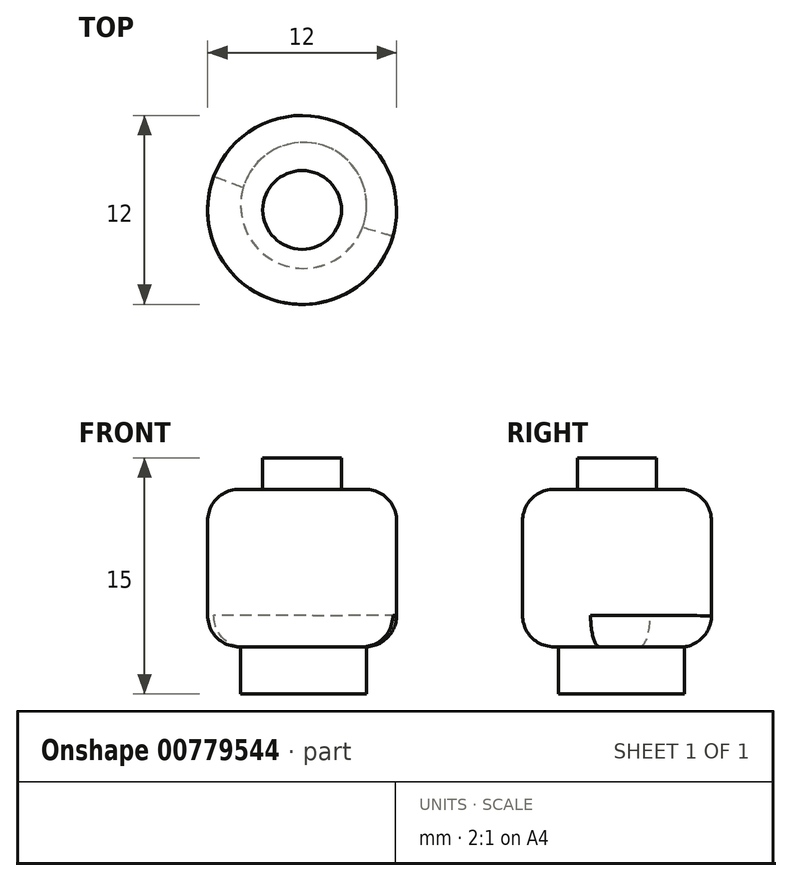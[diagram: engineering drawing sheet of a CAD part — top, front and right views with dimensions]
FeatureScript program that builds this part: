
annotation { "Feature Type Name" : "Feature", "Feature Type Description" : "" }
export const myFeature = defineFeature(function(context is Context, id is Id, definition is map)
    precondition{}
    {
        {
            var Q0;
            Q0=qCreatedBy(makeId("Top.planeOp"),FACE);
            var sketch = newSketch(context, id + "F0", { "sketchPlane" : qUnion([Q0])});
            skCircle(sketch, "E0", {"center": v(0.1, 0.3) * mm, "radius": 4 * mm});
            skSolve(sketch);
        }
        {
            var Q0;
            Q0 = qSketchRegion(id + "F0", true);
            extrude(context, id + "F1", {"entities" : qUnion([Q0]), "endBound" : BoundingType.SYMMETRIC, "depth" : 3 * mm, "offsetDistance" : 25 * mm});
        }
        {
            var Q0;
            Q0=makeQuery(id+"F1.opExtrude","CAP_FACE",FACE,{"disambiguationData":[OSD([sQuery(id+"F0.wireOp",EDGE,"E0")])],"isStart":false});
            var sketch = newSketch(context, id + "F2", { "sketchPlane" : qUnion([Q0])});
            skCircle(sketch, "E1", {"center": v(0, 0) * mm, "radius": 6 * mm});
            skSolve(sketch);
        }
        {
            var Q0;
            Q0 = qSketchRegion(id + "F2", true);
            extrude(context, id + "F3", {"entities" : qUnion([Q0]), "operationType" : NewBodyOperationType.ADD, "depth" : 10 * mm, "offsetDistance" : 25 * mm});
        }
        {
            var Q0;
            Q0=makeQuery(id+"F3.opExtrude","CAP_FACE",FACE,{"disambiguationData":[OSD([sQuery(id+"F2.wireOp",EDGE,"E1")])],"isStart":false});
            var sketch = newSketch(context, id + "F4", { "sketchPlane" : qUnion([Q0])});
            skCircle(sketch, "E2", {"center": v(0, 0) * mm, "radius": 2.5 * mm});
            skSolve(sketch);
        }
        {
            var Q0;
            Q0 = qSketchRegion(id + "F4", true);
            extrude(context, id + "F5", {"entities" : qUnion([Q0]), "operationType" : NewBodyOperationType.ADD, "depth" : 2 * mm, "offsetDistance" : 25 * mm});
        }
        {
            var Q0;
            Q0=makeQuery(id+"F3.opExtrude","CAP_EDGE",EDGE,{"disambiguationData":[OSD([sQuery(id+"F2.wireOp",EDGE,"E1")])],"isStart":true});
            var Q1;
            Q1=makeQuery(id+"F3.opExtrude","CAP_EDGE",EDGE,{"disambiguationData":[OSD([sQuery(id+"F2.wireOp",EDGE,"E1")])],"isStart":false});
            fillet(context, id + "F6", {"entities" : qUnion([Q0, Q1]), "radius" : 2 * mm, "tangentPropagation" : true, "allowEdgeOverflow" : false});
        }
    });
